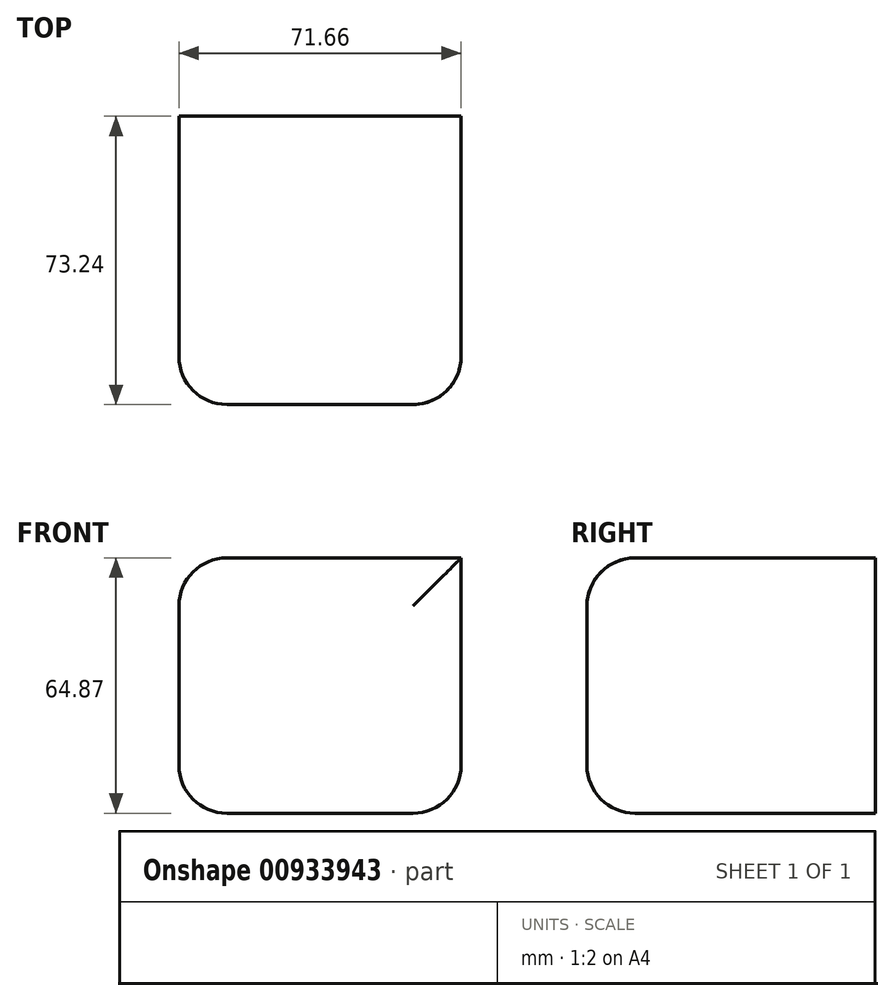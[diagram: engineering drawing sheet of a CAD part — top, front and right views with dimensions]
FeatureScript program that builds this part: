
annotation { "Feature Type Name" : "Feature", "Feature Type Description" : "" }
export const myFeature = defineFeature(function(context is Context, id is Id, definition is map)
    precondition{}
    {
        {
            var Q0;
            Q0=qCreatedBy(makeId("Front.planeOp"),FACE);
            var sketch = newSketch(context, id + "F0", { "sketchPlane" : qUnion([Q0])});
            skLineSegment(sketch, "E0.bottom", {"start": v(-34.43, -32.74) * mm, "end": v(37.23, -32.74) * mm});
            skLineSegment(sketch, "E0.top", {"start": v(-34.43, 32.13) * mm, "end": v(37.23, 32.13) * mm});
            skLineSegment(sketch, "E0.left", {"start": v(-34.43, -32.74) * mm, "end": v(-34.43, 32.13) * mm});
            skLineSegment(sketch, "E0.right", {"start": v(37.23, -32.74) * mm, "end": v(37.23, 32.13) * mm});
            skSolve(sketch);
        }
        {
            var Q0;
            Q0=makeQuery(id+"F0.imprint","IMPRINT",FACE,{"disambiguationData":[TD([[makeQuery(id+"F0.imprint","IMPRINT",EDGE,{"derivedFrom":sQuery(id+"F0.wireOp",EDGE,"E0.bottom")}),1.0]])]});
            var sketch = newSketch(context, id + "F1", { "sketchPlane" : qUnion([Q0])});
            skSolve(sketch);
        }
        {
            var Q0;
            Q0 = qSketchRegion(id + "F1", true);
            var Q1;
            Q1=makeQuery(id+"F1.imprint","IMPRINT",FACE,{"disambiguationData":[TD([[makeQuery(id+"F1.imprint","IMPRINT",EDGE,{"derivedFrom":makeQuery(id+"F0.imprint","IMPRINT",EDGE,{"derivedFrom":sQuery(id+"F0.wireOp",EDGE,"E0.bottom")})}),1.0]])]});
            extrude(context, id + "F2", {"entities" : qUnion([Q0, Q1]), "depth" : 73.24 * mm, "offsetDistance" : 25.4 * mm});
        }
        {
            var Q0;
            Q0=makeQuery(id+"F2.opExtrude","CAP_FACE",FACE,{"disambiguationData":[OSD([sQuery(id+"F0.wireOp",EDGE,"E0.bottom"),sQuery(id+"F0.wireOp",EDGE,"E0.top"),sQuery(id+"F0.wireOp",EDGE,"E0.left"),sQuery(id+"F0.wireOp",EDGE,"E0.right")])],"isStart":false});
            var sketch = newSketch(context, id + "F3", { "sketchPlane" : qUnion([Q0])});
            skCircle(sketch, "E1", {"center": v(0, 0) * mm, "radius": 12.17 * mm});
            skSolve(sketch);
        }
        {
            var Q0;
            Q0=sQuery(id+"F3.wireOp",EDGE,"E1");
            extrude(context, id + "F4", {"bodyType" : ToolBodyType.SURFACE, "surfaceEntities" : qUnion([Q0]), "oppositeDirection" : true, "depth" : 53.63 * mm, "offsetDistance" : 25.4 * mm});
        }
        {
            var Q0;
            Q0=makeQuery(id+"F2.opExtrude","SWEPT_EDGE",EDGE,{"disambiguationData":[OSD([sQuery(id+"F0.wireOp",EDGE,"E0.bottom"),sQuery(id+"F0.wireOp",EDGE,"E0.left")])]});
            var Q1;
            Q1=makeQuery(id+"F2.opExtrude","SWEPT_EDGE",EDGE,{"disambiguationData":[OSD([sQuery(id+"F0.wireOp",EDGE,"E0.bottom"),sQuery(id+"F0.wireOp",EDGE,"E0.right")])]});
            var Q2;
            Q2=makeQuery(id+"F2.opExtrude","SWEPT_EDGE",EDGE,{"disambiguationData":[OSD([sQuery(id+"F0.wireOp",EDGE,"E0.top"),sQuery(id+"F0.wireOp",EDGE,"E0.left")])]});
            var Q3;
            Q3=makeQuery(id+"F2.opExtrude","CAP_EDGE",EDGE,{"disambiguationData":[OSD([sQuery(id+"F0.wireOp",EDGE,"E0.left")])],"isStart":false});
            var Q4;
            Q4=makeQuery(id+"F2.opExtrude","CAP_EDGE",EDGE,{"disambiguationData":[OSD([sQuery(id+"F0.wireOp",EDGE,"E0.top")])],"isStart":false});
            var Q5;
            Q5=makeQuery(id+"F2.opExtrude","CAP_EDGE",EDGE,{"disambiguationData":[OSD([sQuery(id+"F0.wireOp",EDGE,"E0.right")])],"isStart":false});
            var Q6;
            Q6=makeQuery(id+"F2.opExtrude","CAP_EDGE",EDGE,{"disambiguationData":[OSD([sQuery(id+"F0.wireOp",EDGE,"E0.bottom")])],"isStart":false});
            fillet(context, id + "F5", {"entities" : qUnion([Q0, Q1, Q2, Q3, Q4, Q5, Q6]), "radius" : 12.18 * mm, "tangentPropagation" : true, "allowEdgeOverflow" : false});
        }
    });
